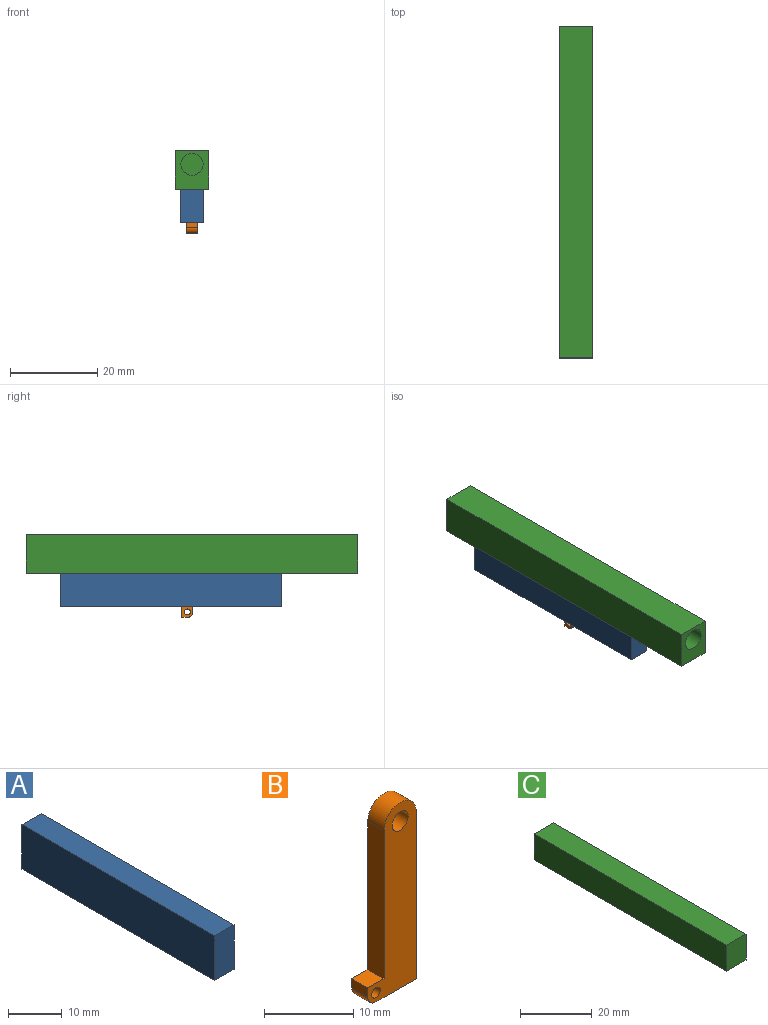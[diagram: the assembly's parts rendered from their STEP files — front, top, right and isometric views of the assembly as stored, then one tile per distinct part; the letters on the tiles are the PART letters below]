
ASSEMBLY  parts=3 mates=2
PART A: 12 faces, bbox 5.1x50.8x10.2 mm
  f0: plane 10.16x5.08mm, normal (0,1,0), area 51.6mm2, adj f1,f3,f4,f5
  f1: plane 50.8x10.16mm, normal (-1,0,0), area 516.1mm2, adj f0,f2,f4,f5
  f2: plane 10.16x5.08mm, normal (0,-1,0), area 51.6mm2, adj f1,f3,f4,f5
  f3: plane 50.8x10.16mm, normal (1,0,0), area 516.1mm2, adj f0,f2,f4,f5
  f4: plane 50.8x5.08mm, normal (0,0,1), area 258.1mm2, adj f0,f1,f2,f3
  f5: plane 50.8x5.08mm, normal (0,0,-1), area 161.3mm2, adj f0,f1,f2,f3,f6,f7,f8,f9
  f6: plane 5.08x2.54mm, normal (0,1,0), area 12.9mm2, adj f5,f7,f9,f10
  f7: plane 38.1x5.08mm, normal (-1,0,0), area 188.5mm2, adj f5,f6,f8,f10,f11
  f8: plane 5.08x2.54mm, normal (0,-1,0), area 12.9mm2, adj f5,f7,f9,f10
  f9: plane 38.1x5.08mm, normal (1,0,0), area 188.5mm2, adj f5,f6,f8,f10,f11
  f10: plane 38.1x2.54mm, normal (0,0,-1), area 96.8mm2, adj f6,f7,f8,f9
  f11: cylinder r=1.27mm len=2.54mm, axis (1,0,0), area 20.3mm2, adj f7,f9
PART B: 11 faces, bbox 7.6x2.5x25.4 mm
  f0: plane 6.35x2.54mm, normal (0,0,-1), area 16.1mm2, adj f2,f3,f7,f9
  f1: plane 2.54x1.27mm, normal (-1,0,0), area 3.2mm2, adj f2,f3,f9,f10
  f2: plane 25.39x7.62mm, normal (0,-1,0), area 125.8mm2, adj f0,f1,f4,f5,f6,f7,f8,f9
  f3: plane 25.39x7.62mm, normal (0,1,0), area 125.8mm2, adj f0,f1,f4,f5,f6,f7,f8,f9
  f4: cylinder r=2.54mm len=5.08mm, axis (0,1,0), area 20.2mm2, adj f2,f3,f5,f7
  f5: plane 20.32x2.54mm, normal (-1,0,0), area 51.6mm2, adj f2,f3,f4,f10
  f6: cylinder r=1.27mm len=2.54mm, axis (0,1,0), area 20.3mm2, adj f2,f3
  f7: plane 22.86x2.54mm, normal (1,0,0), area 58.1mm2, adj f0,f2,f3,f4
  f8: cylinder r=0.68mm len=2.54mm, axis (0,-1,0), area 10.9mm2, adj f2,f3
  f9: cylinder r=1.27mm len=2.54mm, axis (0,-1,0), area 5.1mm2, adj f0,f1,f2,f3
  f10: plane 2.54x2.54mm, normal (0,0,1), area 6.5mm2, adj f1,f2,f3,f5
PART C: 13 faces, bbox 7.6x76.2x8.9 mm
  f0: plane 76.2x8.89mm, normal (-1,0,0), area 677.4mm2, adj f1,f3,f4,f9
  f1: plane 8.89x7.62mm, normal (0,-1,0), area 67.7mm2, adj f0,f2,f4,f9
  f2: plane 76.2x8.89mm, normal (1,0,0), area 677.4mm2, adj f1,f3,f4,f9
  f3: plane 8.89x7.62mm, normal (0,1,0), area 47.5mm2, adj f0,f2,f4,f9,f11
  f4: plane 76.2x7.62mm, normal (0,0,1), area 580.6mm2, adj f0,f1,f2,f3
  f5: plane 5.08x2.54mm, normal (0,1,0), area 12.9mm2, adj f6,f8,f9,f10
  f6: plane 50.8x2.54mm, normal (1,0,0), area 129mm2, adj f5,f7,f9,f10
  f7: plane 5.08x2.54mm, normal (0,-1,0), area 12.9mm2, adj f6,f8,f9,f10
  f8: plane 50.8x2.54mm, normal (-1,0,0), area 129mm2, adj f5,f7,f9,f10
  f9: plane 76.2x7.62mm, normal (0,0,-1), area 322.6mm2, adj f0,f1,f2,f3,f5,f6,f7,f8
  f10: plane 50.8x5.08mm, normal (0,0,-1), area 258.1mm2, adj f5,f6,f7,f8
  f11: cylinder r=2.54mm len=25.4mm, axis (0,1,0), area 405.4mm2, adj f3,f12
  f12: plane 5.08x5.08mm, normal (0,1,0), area 20.3mm2, adj f11
PLACE A t=(-13.84,-9.37,-11.68)mm
PLACE B rot(axis=(-0.58,-0.58,-0.58),120deg) t=(-24.13,6.74,26.19)mm
PLACE C rot(axis=(0,0,1),180deg) t=(-36.63,-10.05,-1.52)mm
MATE planar C.f10 <-> A.f4  axis (0,0,-1) through (-25.4,-14,-1.52)mm
MATE cylindrical B.f6 <-> A.f11  axis (1,0,0) through (-26.67,8.68,-9.14)mm
